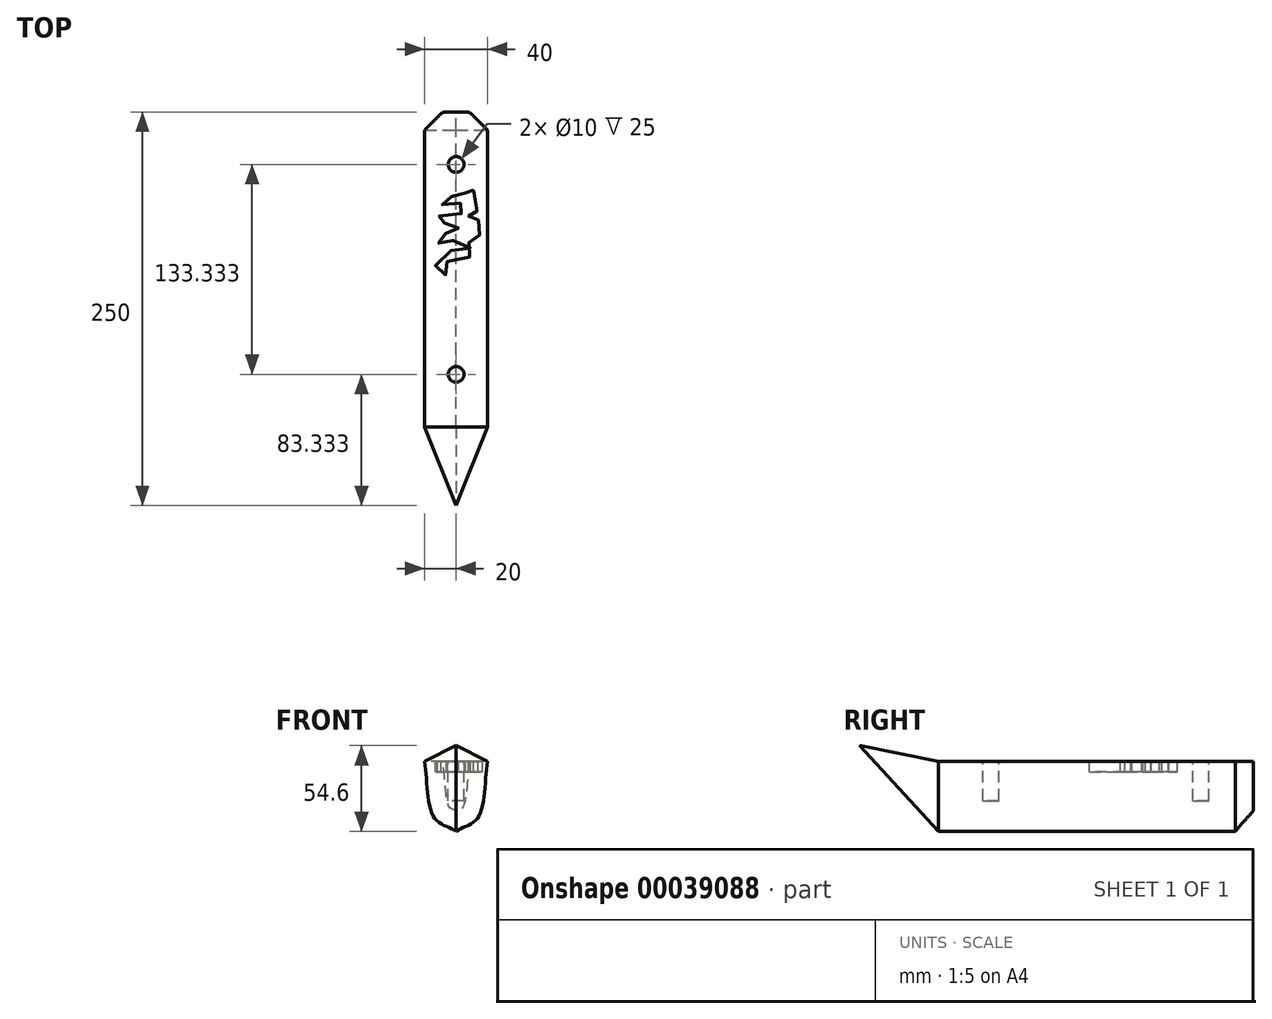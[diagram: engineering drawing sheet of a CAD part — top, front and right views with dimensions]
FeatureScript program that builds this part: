
annotation { "Feature Type Name" : "Feature", "Feature Type Description" : "" }
export const myFeature = defineFeature(function(context is Context, id is Id, definition is map)
    precondition{}
    {
        {
            var Q0;
            Q0=qCreatedBy(makeId("Front.planeOp"),FACE);
            var sketch = newSketch(context, id + "F0", { "sketchPlane" : qUnion([Q0])});
            skLineSegment(sketch, "E0", {"start": v(0, 0) * mm, "end": v(20, 0) * mm});
            skPoint(sketch, "E1", {"position": v(0, -44.6) * mm});
            skFitSpline(sketch, "E2", {"points": [v(20, 0) * mm, v(13.8, -35.8) * mm, v(0, -44.6) * mm], "startDerivative": vector(-9.41, -56.1) * mm, "endDerivative": vector(-31.51, -24) * mm});
            skLineSegment(sketch, "E3.MirrorCS", {"start": v(0, 0) * mm, "end": v(-20, 0) * mm});
            skFitSpline(sketch, "E4.MirrorCS", {"points": [v(-20, 0) * mm, v(-13.8, -35.8) * mm, v(0, -44.6) * mm], "startDerivative": vector(9.41, -56.1) * mm, "endDerivative": vector(31.51, -24) * mm});
            skSolve(sketch);
        }
        {
            var Q0;
            Q0 = qSketchRegion(id + "F0", true);
            extrude(context, id + "F1", {"entities" : qUnion([Q0]), "depth" : 200 * mm});
        }
        {
            var Q0;
            Q0=qCreatedBy(makeId("Front.planeOp"),FACE);
            cPlane(context, id + "F2", {"entities" : qUnion([Q0]), "cplaneType" : CPlaneType.OFFSET, "offset" : 250 * mm, "width" : 150 * mm, "height" : 150 * mm});
        }
        {
            var Q0;
            Q0=qCreatedBy(id+"F2.planeOp",FACE);
            var sketch = newSketch(context, id + "F3", { "sketchPlane" : qUnion([Q0])});
            skPoint(sketch, "E5", {"position": v(0, 10) * mm});
            skSolve(sketch);
        }
        {
            var Q1;
            Q1=makeQuery(id+"F1.opExtrude","CAP_FACE",FACE,{"disambiguationData":[OSD([sQuery(id+"F0.wireOp",EDGE,"E0"),sQuery(id+"F0.wireOp",EDGE,"E2"),sQuery(id+"F0.wireOp",EDGE,"E3.MirrorCS"),sQuery(id+"F0.wireOp",EDGE,"E4.MirrorCS")])],"isStart":false});
            var Q2;
            Q2=sQuery(id+"F3.wireOp",VERTEX,"E5");
            loft(context, id + "F4", {"operationType" : NewBodyOperationType.ADD, "sheetProfilesArray" : [{ "sheetProfileEntities" : qUnion([Q1]) }, { "sheetProfileEntities" : qUnion([Q2]) }]});
        }
        {
            var Q0;
            Q0=makeQuery(id+"F1.opExtrude","SWEPT_FACE",FACE,{"disambiguationData":[OSD([sQuery(id+"F0.wireOp",EDGE,"E0"),sQuery(id+"F0.wireOp",EDGE,"E3.MirrorCS")])]});
            var sketch = newSketch(context, id + "F5", { "sketchPlane" : qUnion([Q0])});
            skLineSegment(sketch, "E6", {"start": v(0, 0) * mm, "end": v(0, -33.33) * mm});
            skLineSegment(sketch, "E7", {"start": v(0, -33.33) * mm, "end": v(0, -166.67) * mm});
            skLineSegment(sketch, "E8", {"start": v(0, -166.67) * mm, "end": v(0, -200) * mm});
            skCircle(sketch, "E9", {"center": v(0, -33.33) * mm, "radius": 5 * mm});
            skCircle(sketch, "E10", {"center": v(0, -166.67) * mm, "radius": 5 * mm});
            skSolve(sketch);
        }
        {
            var Q0;
            Q0 = qSketchRegion(id + "F5", true);
            extrude(context, id + "F6", {"entities" : qUnion([Q0]), "operationType" : NewBodyOperationType.REMOVE, "oppositeDirection" : true, "depth" : 25 * mm});
        }
        {
            var Q0;
            Q0=makeQuery(id+"F1.opExtrude","CAP_EDGE",EDGE,{"disambiguationData":[OSD([sQuery(id+"F0.wireOp",EDGE,"E4.MirrorCS")])],"isStart":true});
            var Q1;
            Q1=makeQuery(id+"F1.opExtrude","CAP_EDGE",EDGE,{"disambiguationData":[OSD([sQuery(id+"F0.wireOp",EDGE,"E2")])],"isStart":true});
            chamfer(context, id + "F7", {"entities" : qUnion([Q0, Q1]), "width" : 11.5 * mm, "tangentPropagation" : true});
        }
        {
            var Q0;
            Q0=qCreatedBy(makeId("Top.planeOp"),FACE);
            var sketch = newSketch(context, id + "F8", { "sketchPlane" : qUnion([Q0])});
            skFitSpline(sketch, "E11", {"points": [v(11.12, -49.52) * mm, v(5.52, -49.6) * mm, v(5.57, -53.47) * mm, v(-8.19, -54.5) * mm, v(-8.12, -59.24) * mm, v(3.91, -58.22) * mm, v(4.85, -63.8) * mm, v(-11.05, -66.16) * mm, v(-11, -70.47) * mm, v(0, -70.78) * mm, v(0, -77.24) * mm, v(-10.47, -77.77) * mm, v(-10.38, -84.23) * mm, v(0, -81.48) * mm, v(9.02, -87) * mm, v(-10.3, -90.25) * mm, v(-10.56, -103.6) * mm, v(-5.42, -101.81) * mm, v(-5.5, -94.93) * mm, v(10.8, -90.84) * mm, v(8.08, -80.98) * mm, v(15.78, -77.44) * mm, v(14.38, -68.85) * mm, v(8.78, -68.06) * mm, v(8.3, -65.05) * mm, v(12.6, -64.14) * mm, v(11.12, -49.52) * mm]});
            skSolve(sketch);
        }
        {
            var Q0;
            Q0 = qSketchRegion(id + "F8", true);
            extrude(context, id + "F9", {"entities" : qUnion([Q0]), "operationType" : NewBodyOperationType.REMOVE, "oppositeDirection" : true, "depth" : 6.58 * mm});
        }
    });
